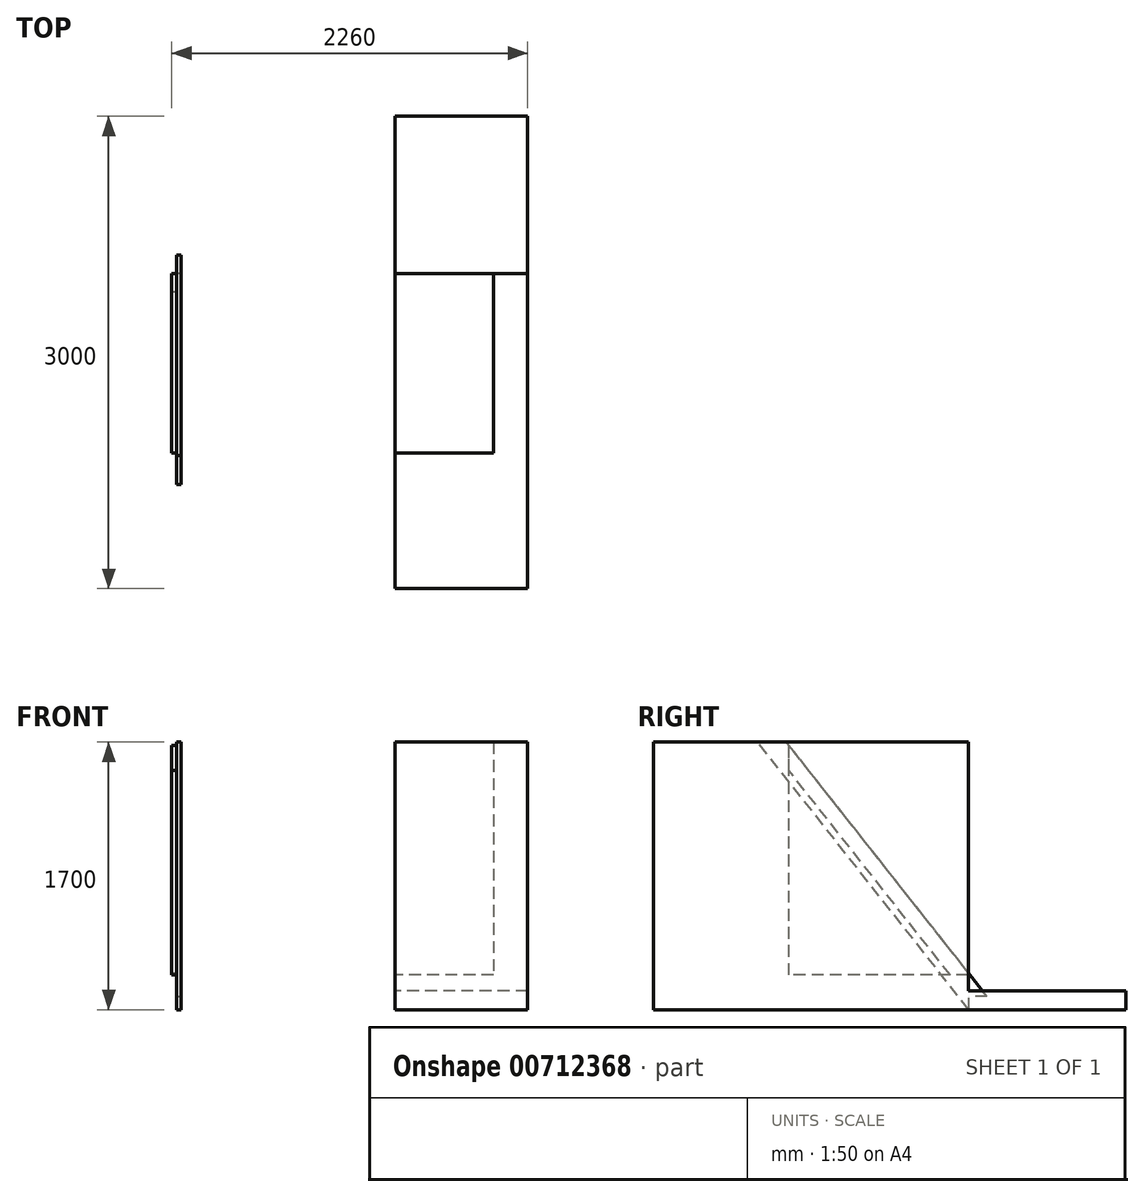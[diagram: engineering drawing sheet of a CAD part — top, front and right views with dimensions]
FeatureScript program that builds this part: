
annotation { "Feature Type Name" : "Feature", "Feature Type Description" : "" }
export const myFeature = defineFeature(function(context is Context, id is Id, definition is map)
    precondition{}
    {
        {
            var Q0;
            Q0=qCreatedBy(makeId("Top.planeOp"),FACE);
            var sketch = newSketch(context, id + "F0", { "sketchPlane" : qUnion([Q0])});
            skLineSegment(sketch, "E0.bottom", {"start": v(0, 0) * mm, "end": v(2000, 0) * mm});
            skLineSegment(sketch, "E0.top", {"start": v(0, 2000) * mm, "end": v(2000, 2000) * mm});
            skLineSegment(sketch, "E0.left", {"start": v(0, 0) * mm, "end": v(0, 2000) * mm});
            skLineSegment(sketch, "E0.right", {"start": v(2000, 0) * mm, "end": v(2000, 2000) * mm});
            skSolve(sketch);
        }
        {
            var Q0;
            Q0 = qSketchRegion(id + "F0", true);
            extrude(context, id + "F1", {"entities" : qUnion([Q0]), "depth" : 1500 * mm, "offsetDistance" : 25 * mm});
        }
        {
            var Q0;
            Q0=makeQuery(id+"F1.opExtrude","SWEPT_FACE",FACE,{"disambiguationData":[OSD([sQuery(id+"F0.wireOp",EDGE,"E0.top")])]});
            var sketch = newSketch(context, id + "F2", { "sketchPlane" : qUnion([Q0])});
            skLineSegment(sketch, "E1.bottom", {"start": v(0, 1500) * mm, "end": v(-1782.87, 1500) * mm});
            skLineSegment(sketch, "E1.top", {"start": v(0, 20) * mm, "end": v(-1782.87, 20) * mm});
            skLineSegment(sketch, "E1.left", {"start": v(0, 1500) * mm, "end": v(0, 20) * mm});
            skLineSegment(sketch, "E1.right", {"start": v(-1782.87, 1500) * mm, "end": v(-1782.87, 20) * mm});
            skSolve(sketch);
        }
        {
            var Q0;
            Q0=makeQuery(id+"F2.imprint","IMPRINT",FACE,{"disambiguationData":[TD([[makeQuery(id+"F2.imprint","IMPRINT",EDGE,{"derivedFrom":sQuery(id+"F2.wireOp",EDGE,"E1.bottom")}),1.0]])]});
            extrude(context, id + "F3", {"entities" : qUnion([Q0]), "operationType" : NewBodyOperationType.REMOVE, "oppositeDirection" : true, "depth" : 1140 * mm, "offsetDistance" : 25 * mm});
        }
        {
            var Q0;
            Q0=makeQuery(id+"F1.opExtrude","SWEPT_FACE",FACE,{"disambiguationData":[OSD([sQuery(id+"F0.wireOp",EDGE,"E0.top")])]});
            var sketch = newSketch(context, id + "F4", { "sketchPlane" : qUnion([Q0])});
            skLineSegment(sketch, "E2.bottom", {"start": v(0, 0) * mm, "end": v(0, 0) * mm});
            skLineSegment(sketch, "E2.top", {"start": v(0, 20) * mm, "end": v(0, 20) * mm});
            skLineSegment(sketch, "E2.left", {"start": v(0, 0) * mm, "end": v(0, 20) * mm});
            skLineSegment(sketch, "E2.right", {"start": v(0, 0) * mm, "end": v(0, 20) * mm});
            skLineSegment(sketch, "E3.bottom", {"start": v(0, 0) * mm, "end": v(-2000, 0) * mm});
            skLineSegment(sketch, "E3.top", {"start": v(0, 20) * mm, "end": v(-2000, 20) * mm});
            skLineSegment(sketch, "E3.right", {"start": v(-2000, 0) * mm, "end": v(-2000, 20) * mm});
            skSolve(sketch);
        }
        {
            var Q0;
            Q0=makeQuery(id+"F4.imprint","IMPRINT",FACE,{"disambiguationData":[TD([[makeQuery(id+"F4.imprint","IMPRINT",EDGE,{"derivedFrom":sQuery(id+"F4.wireOp",EDGE,"E3.bottom")}),-1.0]])]});
            extrude(context, id + "F5", {"entities" : qUnion([Q0]), "operationType" : NewBodyOperationType.ADD, "depth" : 1000 * mm, "offsetDistance" : 25 * mm});
        }
        {
            var Q0;
            Q0=makeQuery(id+"F5.boolean.opBoolean","MERGE",FACE,{"derivedFrom":[makeQuery(id+"F1.opExtrude","CAP_FACE",FACE,{"disambiguationData":[OSD([sQuery(id+"F0.wireOp",EDGE,"E0.bottom"),sQuery(id+"F0.wireOp",EDGE,"E0.top"),sQuery(id+"F0.wireOp",EDGE,"E0.left"),sQuery(id+"F0.wireOp",EDGE,"E0.right")])],"isStart":true}),makeQuery(id+"F5.opExtrude","SWEPT_FACE",FACE,{"disambiguationData":[OSD([sQuery(id+"F4.wireOp",EDGE,"E3.bottom")])]})]});
            extrude(context, id + "F6", {"entities" : qUnion([Q0]), "operationType" : NewBodyOperationType.ADD, "depth" : 200 * mm, "offsetDistance" : 25 * mm});
        }
        {
            var Q0;
            Q0=makeQuery(id+"F5.boolean.opBoolean","MERGE",FACE,{"derivedFrom":[makeQuery(id+"F3.boolean.opBoolean","COPY",FACE,{"derivedFrom":makeQuery(id+"F3.opExtrude","SWEPT_FACE",FACE,{"disambiguationData":[OSD([sQuery(id+"F2.wireOp",EDGE,"E1.top")])]})}),makeQuery(id+"F5.opExtrude","SWEPT_FACE",FACE,{"disambiguationData":[OSD([sQuery(id+"F4.wireOp",EDGE,"E3.top")])]})]});
            var sketch = newSketch(context, id + "F7", { "sketchPlane" : qUnion([Q0])});
            skLineSegment(sketch, "E4.bottom", {"start": v(2000, 3000) * mm, "end": v(0, 3000) * mm});
            skLineSegment(sketch, "E4.top", {"start": v(2000, 2000) * mm, "end": v(0, 2000) * mm});
            skLineSegment(sketch, "E4.left", {"start": v(2000, 3000) * mm, "end": v(2000, 2000) * mm});
            skLineSegment(sketch, "E4.right", {"start": v(0, 3000) * mm, "end": v(0, 2000) * mm});
            skSolve(sketch);
        }
        {
            var Q0;
            Q0=makeQuery(id+"F7.imprint","IMPRINT",FACE,{"disambiguationData":[TD([[makeQuery(id+"F7.imprint","IMPRINT",EDGE,{"derivedFrom":sQuery(id+"F7.wireOp",EDGE,"E4.bottom")}),-1.0]])]});
            extrude(context, id + "F8", {"entities" : qUnion([Q0]), "operationType" : NewBodyOperationType.REMOVE, "oppositeDirection" : true, "depth" : 100 * mm, "offsetDistance" : 25 * mm});
        }
        {
            var Q0;
            {var subQ0=sQuery(id+"F4.wireOp",EDGE,"E2.left");var subQ1=sQuery(id+"F0.wireOp",EDGE,"E0.left");Q0=makeQuery(id+"F6.boolean.opBoolean","MERGE",FACE,{"derivedFrom":[makeQuery(id+"F5.boolean.opBoolean","MERGE",FACE,{"derivedFrom":[makeQuery(id+"F1.opExtrude","SWEPT_FACE",FACE,{"disambiguationData":[OSD([subQ1])]}),makeQuery(id+"F5.opExtrude","SWEPT_FACE",FACE,{"disambiguationData":[OSD([subQ0])]})]}),makeQuery(id+"F6.opExtrude","SWEPT_FACE",FACE,{"disambiguationData":[OSD([subQ1,sQuery(id+"F4.wireOp",EDGE,"E3.bottom"),subQ0])]})]});}
            var sketch = newSketch(context, id + "F9", { "sketchPlane" : qUnion([Q0])});
            skLineSegment(sketch, "E5.bottom", {"start": v(0, -200) * mm, "end": v(-2000, -200) * mm});
            skLineSegment(sketch, "E5.top", {"start": v(0, 1563.28) * mm, "end": v(-2000, 1563.28) * mm});
            skLineSegment(sketch, "E5.left", {"start": v(0, -200) * mm, "end": v(0, 1563.28) * mm});
            skLineSegment(sketch, "E5.right", {"start": v(-2000, -200) * mm, "end": v(-2000, 1563.28) * mm});
            skSolve(sketch);
        }
        {
            var Q0;
            {var subQ4=sQuery(id+"F9.wireOp",EDGE,"E5.top");Q0=makeQuery(id+"F9.imprint","IMPRINT",FACE,{"disambiguationData":[TD([[makeQuery(id+"F9.imprint","IMPRINT",EDGE,{"derivedFrom":subQ4}),1.0]])]});}
            var Q1;
            {var subQ6=sQuery(id+"F9.wireOp",EDGE,"E5.bottom");Q1=makeQuery(id+"F9.imprint","IMPRINT",FACE,{"disambiguationData":[TD([[makeQuery(id+"F9.imprint","IMPRINT",EDGE,{"derivedFrom":subQ6}),-1.0]])]});}
            extrude(context, id + "F10", {"entities" : qUnion([Q0, Q1]), "operationType" : NewBodyOperationType.ADD, "depth" : 200 * mm, "offsetDistance" : 25 * mm});
        }
        {
            var Q0;
            {var subQ0=sQuery(id+"F4.wireOp",EDGE,"E2.left");var subQ1=sQuery(id+"F0.wireOp",EDGE,"E0.left");Q0=makeQuery(id+"F6.boolean.opBoolean","MERGE",FACE,{"derivedFrom":[makeQuery(id+"F5.boolean.opBoolean","MERGE",FACE,{"derivedFrom":[makeQuery(id+"F1.opExtrude","SWEPT_FACE",FACE,{"disambiguationData":[OSD([subQ1])]}),makeQuery(id+"F5.opExtrude","SWEPT_FACE",FACE,{"disambiguationData":[OSD([subQ0])]})]}),makeQuery(id+"F6.opExtrude","SWEPT_FACE",FACE,{"disambiguationData":[OSD([subQ1,sQuery(id+"F4.wireOp",EDGE,"E3.bottom"),subQ0])]})]});}
            var Q1;
            Q1=makeQuery(id+"F10.opExtrude","CAP_FACE",FACE,{"disambiguationData":[OSD([sQuery(id+"F9.wireOp",EDGE,"E5.bottom"),sQuery(id+"F9.wireOp",EDGE,"E5.top"),sQuery(id+"F9.wireOp",EDGE,"E5.left"),sQuery(id+"F9.wireOp",EDGE,"E5.right")])],"isStart":false});
            extrude(context, id + "F11", {"entities" : qUnion([Q0]), "operationType" : NewBodyOperationType.ADD, "endBound" : BoundingType.UP_TO_SURFACE, "depth" : 25 * mm, "endBoundEntityFace" : qUnion([Q1]), "offsetDistance" : 25 * mm});
        }
        {
            var Q0;
            Q0=makeQuery(id+"F10.opExtrude","SWEPT_FACE",FACE,{"disambiguationData":[OSD([sQuery(id+"F9.wireOp",EDGE,"E5.top")])]});
            var Q1;
            Q1=makeQuery(id+"F1.opExtrude","CAP_FACE",FACE,{"disambiguationData":[OSD([sQuery(id+"F0.wireOp",EDGE,"E0.bottom"),sQuery(id+"F0.wireOp",EDGE,"E0.top"),sQuery(id+"F0.wireOp",EDGE,"E0.left"),sQuery(id+"F0.wireOp",EDGE,"E0.right")])],"isStart":false});
            extrude(context, id + "F12", {"entities" : qUnion([Q0]), "operationType" : NewBodyOperationType.REMOVE, "endBound" : BoundingType.UP_TO_SURFACE, "oppositeDirection" : true, "depth" : 25 * mm, "endBoundEntityFace" : qUnion([Q1]), "offsetDistance" : 25 * mm});
        }
        {
            var Q0;
            {var subQ0=sQuery(id+"F9.wireOp",EDGE,"E5.right");var subQ1=sQuery(id+"F9.wireOp",EDGE,"E5.left");var subQ2=sQuery(id+"F9.wireOp",EDGE,"E5.top");var subQ3=sQuery(id+"F9.wireOp",EDGE,"E5.bottom");Q0=makeQuery(id+"F11.boolean.opBoolean","MERGE",FACE,{"derivedFrom":[makeQuery(id+"F10.opExtrude","CAP_FACE",FACE,{"disambiguationData":[OSD([subQ3,subQ2,subQ1,subQ0])],"isStart":false}),makeQuery(id+"F11.opExtrude","CAP_FACE",FACE,{"disambiguationData":[OSD([subQ3,subQ2,subQ1,subQ0])],"isStart":false})]});}
            var sketch = newSketch(context, id + "F13", { "sketchPlane" : qUnion([Q0])});
            skLineSegment(sketch, "E6.bottom", {"start": v(0, -200) * mm, "end": v(-2300, -200) * mm});
            skLineSegment(sketch, "E6.top", {"start": v(0, 2800) * mm, "end": v(-2300, 2800) * mm});
            skLineSegment(sketch, "E6.left", {"start": v(0, -200) * mm, "end": v(0, 2800) * mm});
            skLineSegment(sketch, "E6.right", {"start": v(-2300, -200) * mm, "end": v(-2300, 2800) * mm});
            skLineSegment(sketch, "E7", {"start": v(-2300, -200) * mm, "end": v(-2300, 135.75) * mm});
            skLineSegment(sketch, "E8", {"start": v(-2300, -200) * mm, "end": v(-2185, -200) * mm});
            skLineSegment(sketch, "E9.left", {"start": v(-2300, -200) * mm, "end": v(-2300, -200) * mm});
            skLineSegment(sketch, "E9.right", {"start": v(-2185, -200) * mm, "end": v(-2185, -200) * mm});
            skLineSegment(sketch, "E10.top", {"start": v(-2300, -115) * mm, "end": v(-2185, -115) * mm});
            skLineSegment(sketch, "E10.left", {"start": v(-2300, -200) * mm, "end": v(-2300, -115) * mm});
            skLineSegment(sketch, "E10.right", {"start": v(-2185, -200) * mm, "end": v(-2185, -115) * mm});
            skLineSegment(sketch, "E11", {"start": v(-2300, -115) * mm, "end": v(0, 2800) * mm});
            skLineSegment(sketch, "E12", {"start": v(0, 2654.25) * mm, "end": v(0, 2800) * mm});
            skLineSegment(sketch, "E13", {"start": v(-2185, -200) * mm, "end": v(0, 2569.25) * mm});
            skLineSegment(sketch, "E14", {"start": v(0, 2569.25) * mm, "end": v(0, 2800) * mm});
            skSolve(sketch);
        }
        {
            var Q0;
            {var subQ0=sQuery(id+"F13.wireOp",EDGE,"E14");var subQ1=sQuery(id+"F13.wireOp",EDGE,"E11");var subQ2=makeQuery(id+"F13.imprint","INTERSECT",VERTEX,{"derivedFrom":[sQuery(id+"F13.wireOp",EDGE,"E6.top"),subQ1,subQ0]});Q0=makeQuery(id+"F13.imprint","IMPRINT",FACE,{"disambiguationData":[TD([[makeQuery(id+"F13.imprint","IMPRINT",EDGE,{"disambiguationData":[TD([[subQ2,1.0]])],"derivedFrom":subQ0}),1.0]])]});}
            var Q1;
            {var subQ0=sQuery(id+"F13.wireOp",EDGE,"E11");var subQ1=makeQuery(id+"F10.opExtrude","CAP_EDGE",EDGE,{"disambiguationData":[OSD([sQuery(id+"F9.wireOp",EDGE,"E5.right")])],"isStart":false});var subQ2=makeQuery(id+"F13.imprint","INTERSECT",VERTEX,{"derivedFrom":[subQ1,subQ0]});Q1=makeQuery(id+"F13.imprint","IMPRINT",FACE,{"disambiguationData":[TD([[makeQuery(id+"F13.imprint","IMPRINT",EDGE,{"disambiguationData":[TD([[subQ2,1.0]])],"derivedFrom":subQ1}),-1.0]])]});}
            var Q2;
            {var subQ0=sQuery(id+"F13.wireOp",EDGE,"E11");var subQ1=sQuery(id+"F9.wireOp",EDGE,"E5.right");var subQ4=makeQuery(id+"F10.opExtrude","CAP_EDGE",EDGE,{"disambiguationData":[OSD([subQ1])],"isStart":false});var subQ5=makeQuery(id+"F13.imprint","INTERSECT",VERTEX,{"derivedFrom":[subQ4,subQ0]});Q2=makeQuery(id+"F13.imprint","IMPRINT",FACE,{"disambiguationData":[TD([[makeQuery(id+"F13.imprint","IMPRINT",EDGE,{"disambiguationData":[TD([[subQ5,1.0]])],"derivedFrom":subQ4}),1.0]])]});}
            var Q3;
            {var subQ1=sQuery(id+"F13.wireOp",EDGE,"E10.top");Q3=makeQuery(id+"F13.imprint","IMPRINT",FACE,{"disambiguationData":[TD([[makeQuery(id+"F13.imprint","IMPRINT",EDGE,{"derivedFrom":subQ1}),1.0]])]});}
            var Q4;
            Q4=makeQuery(id+"F13.imprint","IMPRINT",FACE,{"disambiguationData":[TD([[makeQuery(id+"F13.imprint","IMPRINT",EDGE,{"derivedFrom":sQuery(id+"F13.wireOp",EDGE,"E8")}),-1.0]])]});
            extrude(context, id + "F14", {"entities" : qUnion([Q0, Q1, Q2, Q3, Q4]), "depth" : 30 * mm, "offsetDistance" : 25 * mm});
        }
        {
            var Q0;
            Q0=makeQuery(id+"F14.opExtrude","SWEPT_BODY",BODY,{"disambiguationData":[OSD([sQuery(id+"F13.wireOp",EDGE,"E8"),sQuery(id+"F13.wireOp",EDGE,"E10.left"),sQuery(id+"F13.wireOp",EDGE,"E11"),sQuery(id+"F13.wireOp",EDGE,"E13"),sQuery(id+"F13.wireOp",EDGE,"E14")])]});
            var Q1;
            Q1=makeQuery(id+"F14.opExtrude","CAP_VERTEX",VERTEX,{"disambiguationData":[OSD([sQuery(id+"F0.wireOp",EDGE,"E0.left"),sQuery(id+"F4.wireOp",EDGE,"E3.bottom"),sQuery(id+"F4.wireOp",EDGE,"E2.left"),sQuery(id+"F9.wireOp",EDGE,"E5.bottom"),sQuery(id+"F9.wireOp",EDGE,"E5.top"),sQuery(id+"F9.wireOp",EDGE,"E5.left"),sQuery(id+"F9.wireOp",EDGE,"E5.right"),sQuery(id+"F13.wireOp",EDGE,"E8"),sQuery(id+"F13.wireOp",EDGE,"E10.left")])],"isStart":true});
            var Q2;
            Q2=makeQuery(id+"F3.boolean.opBoolean","COPY",VERTEX,{"derivedFrom":makeQuery(id+"F3.opExtrude","CAP_VERTEX",VERTEX,{"disambiguationData":[OSD([sQuery(id+"F2.wireOp",EDGE,"E1.top"),sQuery(id+"F2.wireOp",EDGE,"E1.right")])],"isStart":true})});
            transform(context, id + "F15", {"entities" : qUnion([Q0]), "transformType" : TransformType.TRANSLATION_ENTITY, "oppositeDirectionEntity" : false, "transformLine" : qUnion([Q1, Q2]), "makeCopy" : false});
        }
        {
            var Q0;
            {var subQ0=sQuery(id+"F9.wireOp",EDGE,"E5.right");var subQ1=sQuery(id+"F9.wireOp",EDGE,"E5.left");var subQ2=sQuery(id+"F9.wireOp",EDGE,"E5.top");var subQ3=sQuery(id+"F9.wireOp",EDGE,"E5.bottom");Q0=makeQuery(id+"F11.boolean.opBoolean","MERGE",FACE,{"derivedFrom":[makeQuery(id+"F10.opExtrude","CAP_FACE",FACE,{"disambiguationData":[OSD([subQ3,subQ2,subQ1,subQ0])],"isStart":false}),makeQuery(id+"F11.opExtrude","CAP_FACE",FACE,{"disambiguationData":[OSD([subQ3,subQ2,subQ1,subQ0])],"isStart":false})]});}
            extrude(context, id + "F16", {"entities" : qUnion([Q0]), "operationType" : NewBodyOperationType.REMOVE, "oppositeDirection" : true, "depth" : 1360 * mm, "offsetDistance" : 25 * mm});
        }
        {
            var Q0;
            Q0=makeQuery(id+"F14.opExtrude","CAP_FACE",FACE,{"disambiguationData":[OSD([sQuery(id+"F13.wireOp",EDGE,"E8"),sQuery(id+"F13.wireOp",EDGE,"E10.left"),sQuery(id+"F13.wireOp",EDGE,"E11"),sQuery(id+"F13.wireOp",EDGE,"E13"),sQuery(id+"F13.wireOp",EDGE,"E14")])],"isStart":false});
            var sketch = newSketch(context, id + "F17", { "sketchPlane" : qUnion([Q0])});
            skLineSegment(sketch, "E15.0", {"start": v(-860, 20) * mm, "end": v(-860, 1500) * mm});
            skLineSegment(sketch, "E16.0", {"start": v(-860, 1500) * mm, "end": v(-2000, 1500) * mm});
            skLineSegment(sketch, "E17", {"start": v(-1885, 20) * mm, "end": v(-860, 1319.08) * mm});
            skLineSegment(sketch, "E18", {"start": v(-2000, 105) * mm, "end": v(-899.31, 1500) * mm});
            skLineSegment(sketch, "E19", {"start": v(-899.31, 1500) * mm, "end": v(-860, 1500) * mm});
            skLineSegment(sketch, "E20", {"start": v(-860, 1500) * mm, "end": v(-860, 1319.08) * mm});
            skLineSegment(sketch, "E21", {"start": v(-2000, 105) * mm, "end": v(-2000, 20) * mm});
            skLineSegment(sketch, "E22", {"start": v(-2000, 20) * mm, "end": v(-1885, 20) * mm});
            skSolve(sketch);
        }
        {
            var Q0;
            Q0=makeQuery(id+"F17.imprint","IMPRINT",FACE,{"disambiguationData":[TD([[makeQuery(id+"F17.imprint","IMPRINT",EDGE,{"derivedFrom":sQuery(id+"F17.wireOp",EDGE,"E17")}),1.0]])]});
            extrude(context, id + "F18", {"entities" : qUnion([Q0]), "depth" : 30 * mm, "offsetDistance" : 25 * mm});
        }
    });
